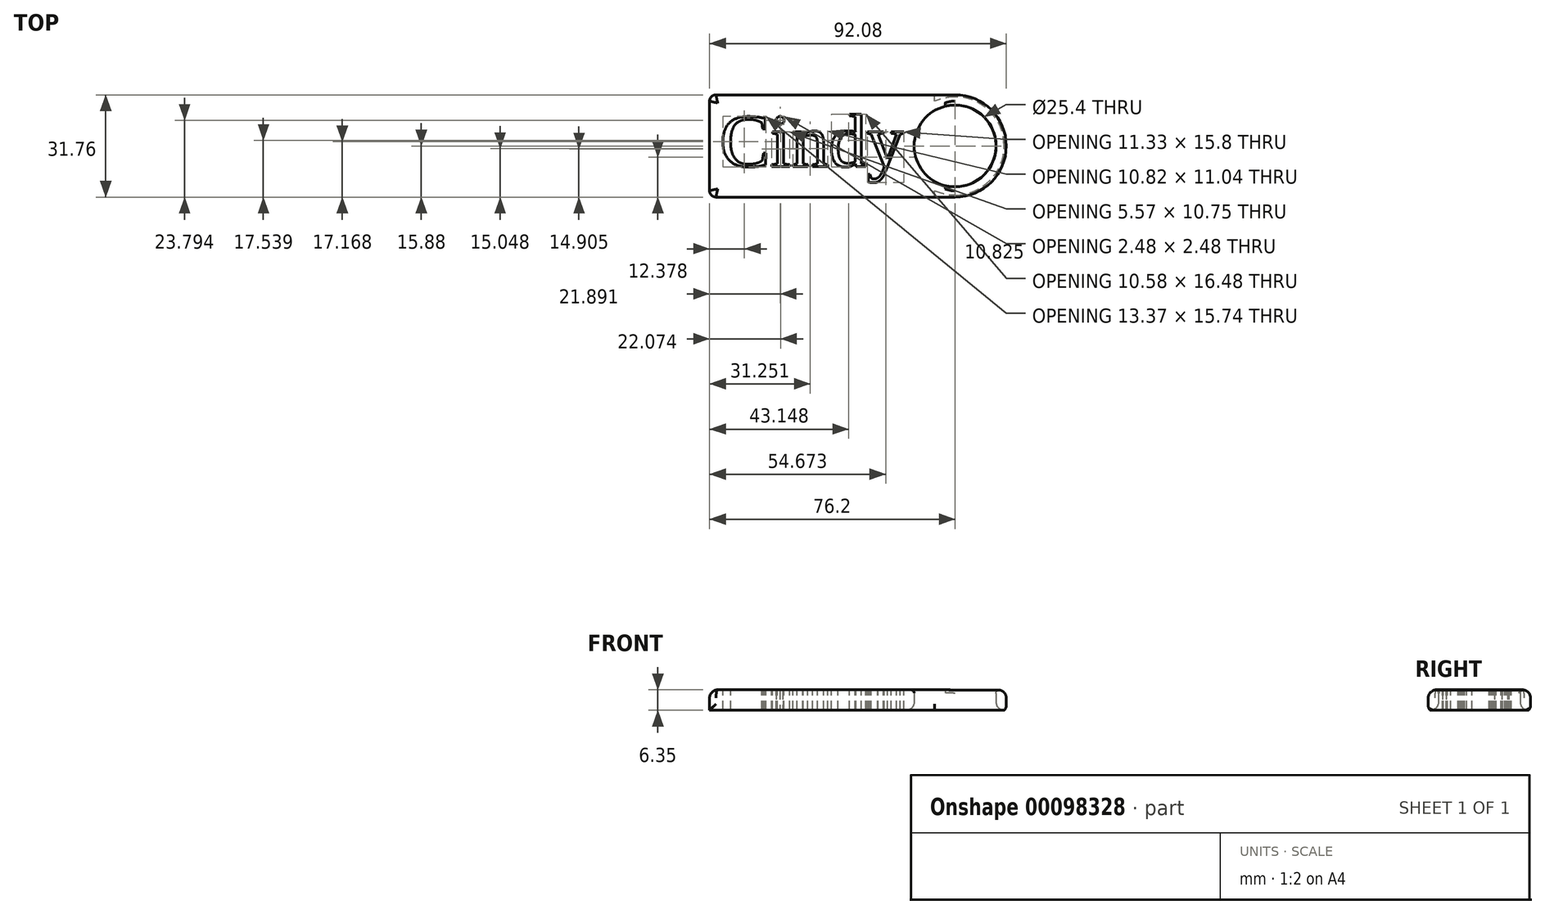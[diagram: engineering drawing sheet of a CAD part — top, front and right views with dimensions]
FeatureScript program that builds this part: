
annotation { "Feature Type Name" : "Feature", "Feature Type Description" : "" }
export const myFeature = defineFeature(function(context is Context, id is Id, definition is map)
    precondition{}
    {
        {
            var Q0;
            Q0=qCreatedBy(makeId("Top.planeOp"),FACE);
            var sketch = newSketch(context, id + "F0", { "sketchPlane" : qUnion([Q0])});
            skLineSegment(sketch, "E0.bottom", {"start": v(-38.1, 15.88) * mm, "end": v(38.1, 15.88) * mm});
            skLineSegment(sketch, "E0.top", {"start": v(-38.1, -15.88) * mm, "end": v(38.1, -15.88) * mm});
            skLineSegment(sketch, "E0.left", {"start": v(-38.1, 15.88) * mm, "end": v(-38.1, -15.87) * mm});
            skLineSegment(sketch, "E0.right", {"start": v(38.1, 15.88) * mm, "end": v(38.1, -15.87) * mm});
            skPoint(sketch, "E0.middle", {"position": v(0, 0) * mm});
            skCircle(sketch, "E1", {"center": v(38.1, 0) * mm, "radius": 15.88 * mm});
            skCircle(sketch, "E2", {"center": v(38.1, 0) * mm, "radius": 12.7 * mm});
            skSolve(sketch);
        }
        {
            var Q0;
            Q0 = qSketchRegion(id + "F0", true);
            extrude(context, id + "F1", {"entities" : qUnion([Q0]), "depth" : 6.35 * mm});
        }
        {
            var Q0;
            Q0=makeQuery(id+"F1.opExtrude","CAP_FACE",FACE,{"disambiguationData":[OSD([sQuery(id+"F0.wireOp",EDGE,"E0.bottom"),sQuery(id+"F0.wireOp",EDGE,"E0.top"),sQuery(id+"F0.wireOp",EDGE,"E0.left"),sQuery(id+"F0.wireOp",EDGE,"E1"),sQuery(id+"F0.wireOp",EDGE,"E2")])],"isStart":false});
            var sketch = newSketch(context, id + "F2", { "sketchPlane" : qUnion([Q0])});
            skText(sketch, "E3", { "text": "Cindy", "fontName": "Tinos-Regular.ttf"});
            const initialGuessF2  = {"E3": [-0.03492, -0.00635, 1, 0, 0.01686]};
            skSetInitialGuess(sketch, initialGuessF2);
            skSolve(sketch);
        }
        {
            var Q0;
            Q0 = qSketchRegion(id + "F2", true);
            extrude(context, id + "F3", {"entities" : qUnion([Q0]), "operationType" : NewBodyOperationType.REMOVE, "endBound" : BoundingType.THROUGH_ALL, "oppositeDirection" : true, "depth" : 3 * mm});
        }
        {
            var Q0;
            Q0=makeQuery(id+"F1.opExtrude","CAP_EDGE",EDGE,{"disambiguationData":[OSD([sQuery(id+"F0.wireOp",EDGE,"E0.left")])],"isStart":true});
            fillet(context, id + "F4", {"entities" : qUnion([Q0]), "radius" : 0.1 * mm, "tangentPropagation" : true, "allowEdgeOverflow" : false});
        }
        {
            var Q0;
            Q0=makeQuery(id+"F1.opExtrude","CAP_EDGE",EDGE,{"disambiguationData":[OSD([sQuery(id+"F0.wireOp",EDGE,"E1")])],"isStart":false});
            var Q1;
            Q1=makeQuery(id+"F1.opExtrude","CAP_EDGE",EDGE,{"disambiguationData":[OSD([sQuery(id+"F0.wireOp",EDGE,"E0.left")])],"isStart":false});
            fillet(context, id + "F5", {"entities" : qUnion([Q0, Q1]), "radius" : 2.54 * mm, "tangentPropagation" : true, "allowEdgeOverflow" : false});
        }
        {
            var Q0;
            Q0=makeQuery(id+"F1.opExtrude","CAP_EDGE",EDGE,{"disambiguationData":[OSD([sQuery(id+"F0.wireOp",EDGE,"E2")])],"isStart":true});
            fillet(context, id + "F6", {"entities" : qUnion([Q0]), "radius" : 2.54 * mm, "tangentPropagation" : true, "allowEdgeOverflow" : false});
        }
        {
            var Q0;
            Q0=makeQuery(id+"F1.opExtrude","CAP_EDGE",EDGE,{"disambiguationData":[OSD([sQuery(id+"F0.wireOp",EDGE,"E2")])],"isStart":false});
            fillet(context, id + "F7", {"entities" : qUnion([Q0]), "radius" : 1 * mm, "tangentPropagation" : true, "allowEdgeOverflow" : false});
        }
        {
            var Q0;
            Q0=makeQuery(id+"F1.opExtrude","CAP_EDGE",EDGE,{"disambiguationData":[OSD([sQuery(id+"F0.wireOp",EDGE,"E0.top")])],"isStart":true});
            fillet(context, id + "F8", {"entities" : qUnion([Q0]), "radius" : 2 * mm, "tangentPropagation" : true, "allowEdgeOverflow" : false});
        }
    });
